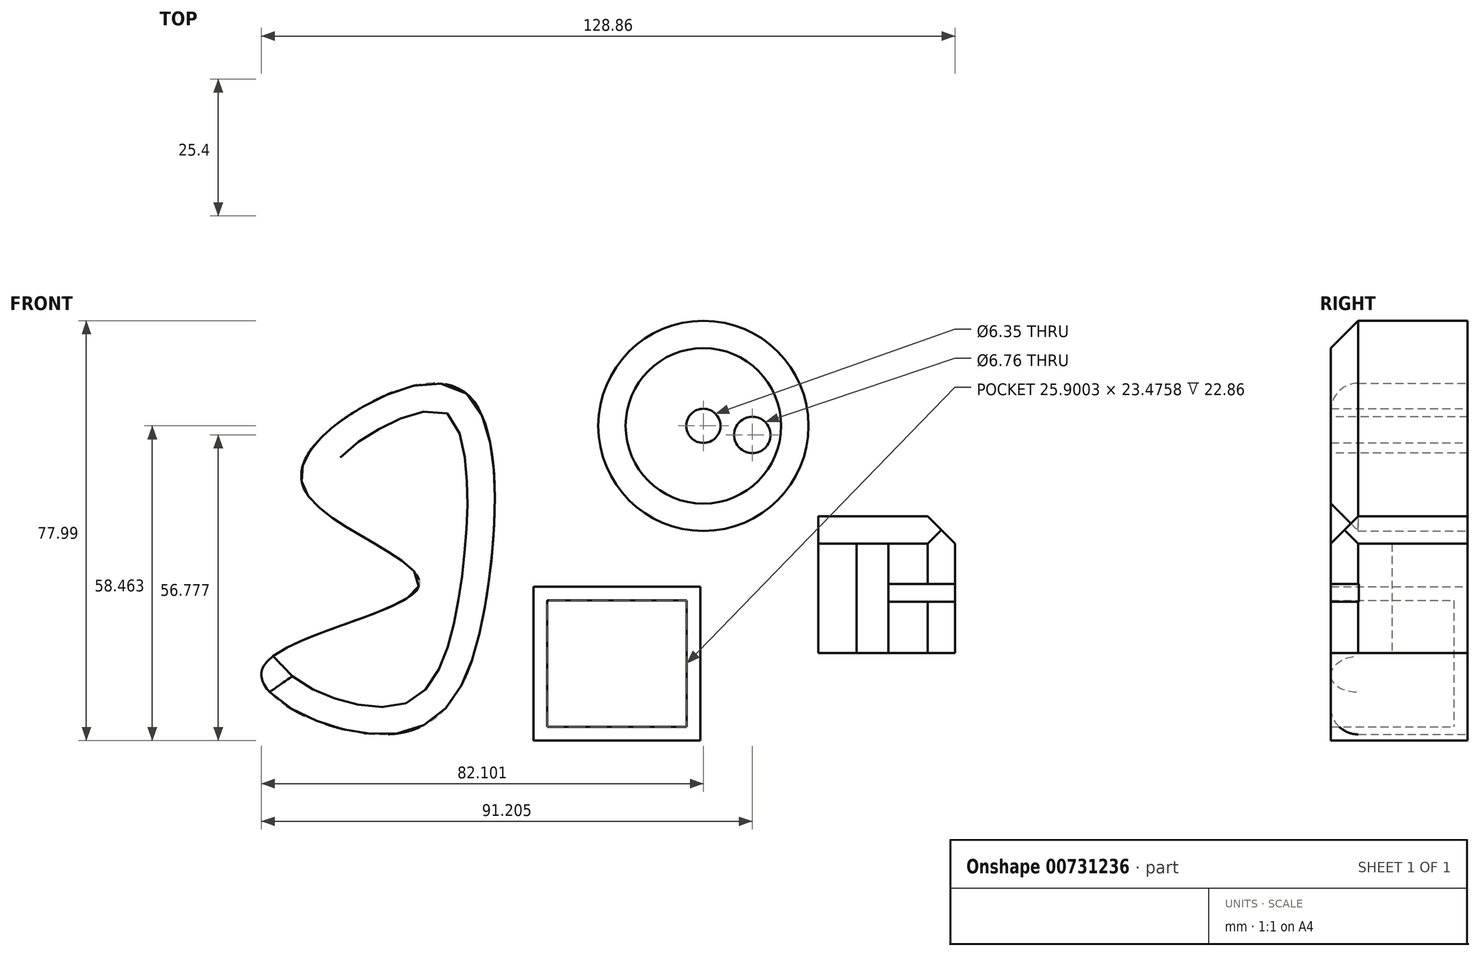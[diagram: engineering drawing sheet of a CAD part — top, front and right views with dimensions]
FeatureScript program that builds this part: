
annotation { "Feature Type Name" : "Feature", "Feature Type Description" : "" }
export const myFeature = defineFeature(function(context is Context, id is Id, definition is map)
    precondition{}
    {
        {
            var Q0;
            Q0=qCreatedBy(makeId("Front.planeOp"),FACE);
            var sketch = newSketch(context, id + "F0", { "sketchPlane" : qUnion([Q0])});
            skLineSegment(sketch, "E0.bottom", {"start": v(-16.3, 15.22) * mm, "end": v(14.68, 15.22) * mm});
            skLineSegment(sketch, "E0.top", {"start": v(-16.3, -13.34) * mm, "end": v(14.68, -13.34) * mm});
            skLineSegment(sketch, "E0.left", {"start": v(-16.3, 15.22) * mm, "end": v(-16.3, -13.34) * mm});
            skLineSegment(sketch, "E0.right", {"start": v(14.68, 15.22) * mm, "end": v(14.68, -13.34) * mm});
            skCircle(sketch, "E1", {"center": v(15.22, 45.12) * mm, "radius": 19.52 * mm});
            skFitSpline(sketch, "E2", {"points": [v(-48.09, 48.63) * mm, v(-58.6, 32.73) * mm, v(-37.58, 15.5) * mm, v(-66.67, 0) * mm, v(-41.35, -11.99) * mm, v(-24.65, 16.03) * mm, v(-28.7, 51.05) * mm, v(-48.09, 48.63) * mm]});
            skSolve(sketch);
        }
        {
            var Q0;
            Q0=makeQuery(id+"F0.imprint","IMPRINT",FACE,{"disambiguationData":[TD([[makeQuery(id+"F0.imprint","IMPRINT",EDGE,{"derivedFrom":sQuery(id+"F0.wireOp",EDGE,"E1")}),1.0]])]});
            var Q1;
            Q1=makeQuery(id+"F0.imprint","IMPRINT",FACE,{"disambiguationData":[TD([[makeQuery(id+"F0.imprint","IMPRINT",EDGE,{"derivedFrom":sQuery(id+"F0.wireOp",EDGE,"E2")}),1.0]])]});
            var Q2;
            Q2=makeQuery(id+"F0.imprint","IMPRINT",FACE,{"disambiguationData":[TD([[makeQuery(id+"F0.imprint","IMPRINT",EDGE,{"derivedFrom":sQuery(id+"F0.wireOp",EDGE,"E0.bottom")}),-1.0]])]});
            extrude(context, id + "F1", {"entities" : qUnion([Q0, Q1, Q2]), "depth" : 25.4 * mm, "offsetDistance" : 25.4 * mm});
        }
        {
            var Q0;
            Q0=makeQuery(id+"F1.opExtrude","CAP_FACE",FACE,{"disambiguationData":[OSD([sQuery(id+"F0.wireOp",EDGE,"E2")])],"isStart":false});
            fillet(context, id + "F2", {"entities" : qUnion([Q0]), "radius" : 5.08 * mm, "tangentPropagation" : true, "allowEdgeOverflow" : false});
        }
        {
            var Q0;
            Q0=makeQuery(id+"F1.opExtrude","CAP_FACE",FACE,{"disambiguationData":[OSD([sQuery(id+"F0.wireOp",EDGE,"E1")])],"isStart":false});
            chamfer(context, id + "F3", {"entities" : qUnion([Q0]), "width" : 5.08 * mm, "tangentPropagation" : true});
        }
        {
            var Q0;
            Q0=sQuery(id+"F0.wireOp",VERTEX,"E1.center");
            var Q1;
            Q1=makeQuery(id+"F1.opExtrude","SWEPT_BODY",BODY,{"disambiguationData":[OSD([sQuery(id+"F0.wireOp",EDGE,"E1")])]});
            hole(context, id + "F4", {"style" : HoleStyle.SIMPLE, "endStyle" : HoleEndStyle.THROUGH, "oppositeDirection" : true, "holeDiameter" : 6.35 * mm, "majorDiameter" : 6.35 * mm, "isTappedThrough" : true, "tappedDepth" : 12.7 * mm, "tapClearance" : 3, "locations" : qUnion([Q0]), "scope" : qUnion([Q1])});
        }
        {
            var Q0;
            Q0=makeQuery(id+"F1.opExtrude","CAP_FACE",FACE,{"disambiguationData":[OSD([sQuery(id+"F0.wireOp",EDGE,"E1")])],"isStart":false});
            var sketch = newSketch(context, id + "F5", { "sketchPlane" : qUnion([Q0])});
            skPoint(sketch, "E3", {"position": v(24.32, 43.44) * mm});
            skSolve(sketch);
        }
        {
            var Q0;
            Q0=sQuery(id+"F5.wireOp",VERTEX,"E3");
            var Q1;
            Q1=makeQuery(id+"F1.opExtrude","SWEPT_BODY",BODY,{"disambiguationData":[OSD([sQuery(id+"F0.wireOp",EDGE,"E1")])]});
            hole(context, id + "F6", {"style" : HoleStyle.SIMPLE, "endStyle" : HoleEndStyle.THROUGH, "holeDiameter" : 6.76 * mm, "majorDiameter" : 6.35 * mm, "isTappedThrough" : true, "tappedDepth" : 12.7 * mm, "tapClearance" : 3, "locations" : qUnion([Q0]), "scope" : qUnion([Q1])});
        }
        {
            var Q0;
            Q0=makeQuery(id+"F1.opExtrude","CAP_FACE",FACE,{"disambiguationData":[OSD([sQuery(id+"F0.wireOp",EDGE,"E0.bottom"),sQuery(id+"F0.wireOp",EDGE,"E0.top"),sQuery(id+"F0.wireOp",EDGE,"E0.left"),sQuery(id+"F0.wireOp",EDGE,"E0.right")])],"isStart":false});
            shell(context, id + "F7", {"entities" : qUnion([Q0]), "thickness" : 2.54 * mm});
        }
        {
            var Q0;
            Q0=qCreatedBy(makeId("Front.planeOp"),FACE);
            var sketch = newSketch(context, id + "F8", { "sketchPlane" : qUnion([Q0])});
            skLineSegment(sketch, "E4.bottom", {"start": v(36.58, 28.33) * mm, "end": v(61.98, 28.33) * mm});
            skLineSegment(sketch, "E4.top", {"start": v(36.58, 2.93) * mm, "end": v(61.98, 2.93) * mm});
            skLineSegment(sketch, "E4.left", {"start": v(36.58, 28.33) * mm, "end": v(36.58, 2.93) * mm});
            skLineSegment(sketch, "E4.right", {"start": v(61.98, 28.33) * mm, "end": v(61.98, 2.93) * mm});
            skSolve(sketch);
        }
        {
            var Q0;
            Q0 = qSketchRegion(id + "F8", true);
            extrude(context, id + "F9", {"entities" : qUnion([Q0]), "depth" : 25.4 * mm, "offsetDistance" : 25.4 * mm});
        }
        {
            var Q0;
            Q0=makeQuery(id+"F9.opExtrude","SWEPT_EDGE",EDGE,{"disambiguationData":[OSD([sQuery(id+"F8.wireOp",EDGE,"E4.bottom"),sQuery(id+"F8.wireOp",EDGE,"E4.right")])]});
            chamfer(context, id + "F10", {"entities" : qUnion([Q0]), "width" : 5.08 * mm, "tangentPropagation" : true});
        }
        {
            var Q0;
            Q0=makeQuery(id+"F9.opExtrude","CAP_EDGE",EDGE,{"disambiguationData":[OSD([sQuery(id+"F8.wireOp",EDGE,"E4.bottom")])],"isStart":false});
            chamfer(context, id + "F11", {"entities" : qUnion([Q0]), "width" : 5.08 * mm, "tangentPropagation" : true});
        }
        {
            var Q0;
            Q0=makeQuery(id+"F9.opExtrude","CAP_EDGE",EDGE,{"disambiguationData":[OSD([sQuery(id+"F8.wireOp",EDGE,"E4.right")])],"isStart":false});
            chamfer(context, id + "F12", {"entities" : qUnion([Q0]), "width" : 5.08 * mm, "tangentPropagation" : true});
        }
        {
            var Q0;
            Q0=makeQuery(id+"F9.opExtrude","CAP_FACE",FACE,{"disambiguationData":[OSD([sQuery(id+"F8.wireOp",EDGE,"E4.bottom"),sQuery(id+"F8.wireOp",EDGE,"E4.top"),sQuery(id+"F8.wireOp",EDGE,"E4.left"),sQuery(id+"F8.wireOp",EDGE,"E4.right")])],"isStart":false});
            var sketch = newSketch(context, id + "F13", { "sketchPlane" : qUnion([Q0])});
            skLineSegment(sketch, "E5.bottom", {"start": v(43.7, 23.25) * mm, "end": v(49.57, 23.25) * mm});
            skLineSegment(sketch, "E5.top", {"start": v(43.7, 2.93) * mm, "end": v(49.57, 2.93) * mm});
            skLineSegment(sketch, "E5.left", {"start": v(43.7, 23.25) * mm, "end": v(43.7, 2.93) * mm});
            skLineSegment(sketch, "E5.right", {"start": v(49.57, 23.25) * mm, "end": v(49.57, 2.93) * mm});
            skSolve(sketch);
        }
        {
            var Q0;
            Q0=makeQuery(id+"F13.imprint","IMPRINT",FACE,{"disambiguationData":[TD([[makeQuery(id+"F13.imprint","IMPRINT",EDGE,{"derivedFrom":sQuery(id+"F13.wireOp",EDGE,"E5.bottom")}),1.0]])]});
            extrude(context, id + "F14", {"entities" : qUnion([Q0]), "operationType" : NewBodyOperationType.REMOVE, "oppositeDirection" : true, "depth" : 11.32 * mm, "offsetDistance" : 25.4 * mm});
        }
        {
            var Q0;
            {var subQ0=sQuery(id+"F8.wireOp",EDGE,"E4.bottom");var subQ1=sQuery(id+"F8.wireOp",EDGE,"E4.right");var subQ2=sQuery(id+"F8.wireOp",EDGE,"E4.top");Q0=makeQuery(id+"F14.boolean.opBoolean","SPLIT",FACE,{"disambiguationData":[TD([makeQuery(id+"F12.opChamfer","BLEND_FACE",FACE,{"disambiguationData":[OSD([subQ1])]})])],"derivedFrom":makeQuery(id+"F9.opExtrude","CAP_FACE",FACE,{"disambiguationData":[OSD([subQ0,subQ2,sQuery(id+"F8.wireOp",EDGE,"E4.left"),subQ1])],"isStart":false})});}
            var sketch = newSketch(context, id + "F15", { "sketchPlane" : qUnion([Q0])});
            skLineSegment(sketch, "E6.bottom", {"start": v(49.57, 15.74) * mm, "end": v(63, 15.74) * mm});
            skLineSegment(sketch, "E6.top", {"start": v(49.57, 12.48) * mm, "end": v(63, 12.48) * mm});
            skLineSegment(sketch, "E6.left", {"start": v(49.57, 15.74) * mm, "end": v(49.57, 12.48) * mm});
            skLineSegment(sketch, "E6.right", {"start": v(63, 15.74) * mm, "end": v(63, 12.48) * mm});
            skSolve(sketch);
        }
        {
            var Q0;
            {var subQ0=sQuery(id+"F15.wireOp",EDGE,"E6.right");Q0=makeQuery(id+"F15.imprint","IMPRINT",FACE,{"disambiguationData":[TD([[makeQuery(id+"F15.imprint","IMPRINT",EDGE,{"derivedFrom":subQ0}),-1.0]])]});}
            var Q1;
            {var subQ0=sQuery(id+"F15.wireOp",EDGE,"E6.left");Q1=makeQuery(id+"F15.imprint","IMPRINT",FACE,{"disambiguationData":[TD([[makeQuery(id+"F15.imprint","IMPRINT",EDGE,{"derivedFrom":subQ0}),1.0]])]});}
            extrude(context, id + "F16", {"entities" : qUnion([Q0, Q1]), "operationType" : NewBodyOperationType.REMOVE, "oppositeDirection" : true, "depth" : 5.17 * mm, "offsetDistance" : 25.4 * mm});
        }
    });
